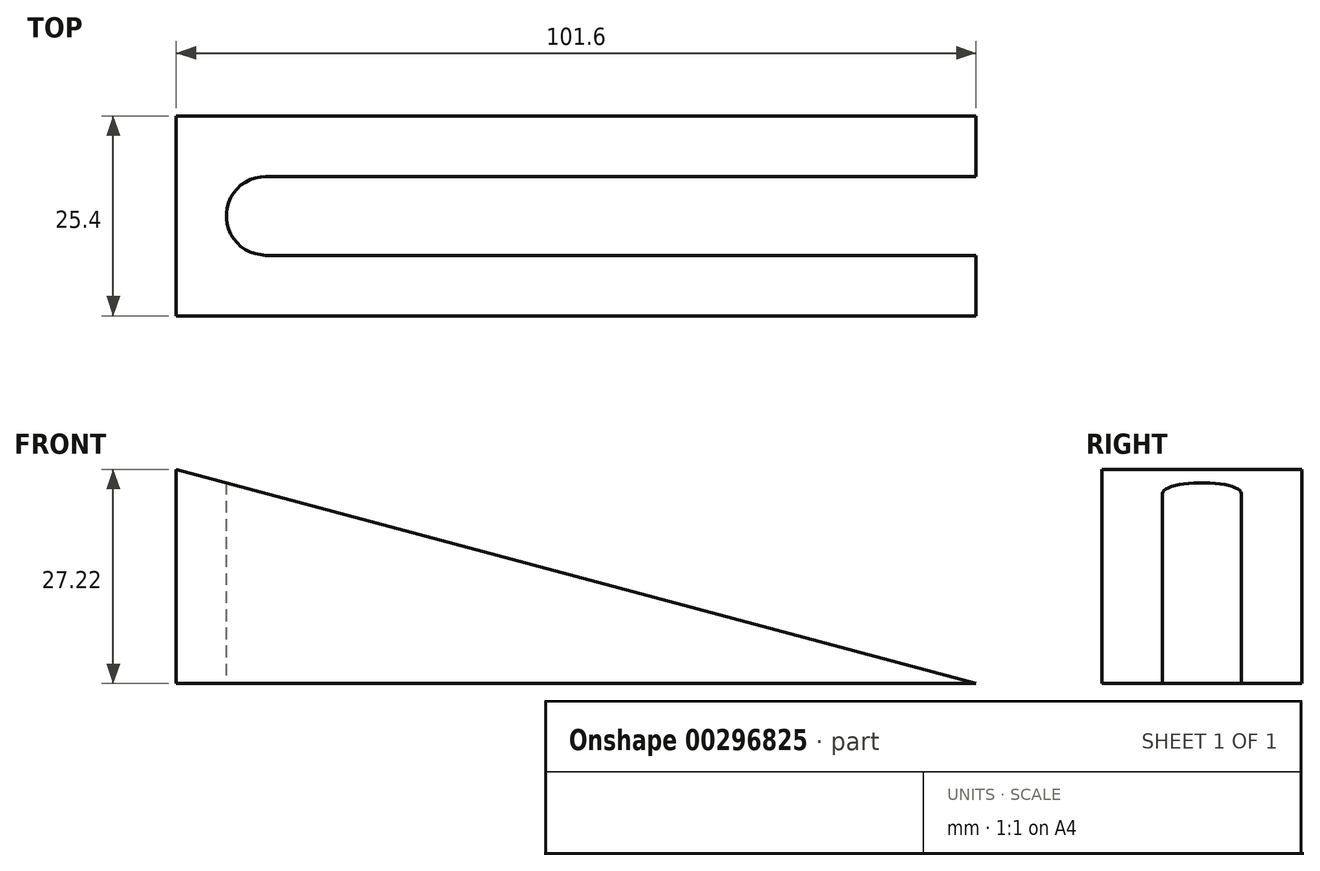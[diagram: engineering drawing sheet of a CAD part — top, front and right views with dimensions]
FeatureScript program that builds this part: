
annotation { "Feature Type Name" : "Feature", "Feature Type Description" : "" }
export const myFeature = defineFeature(function(context is Context, id is Id, definition is map)
    precondition{}
    {
        {
            var Q0;
            Q0=qCreatedBy(makeId("Front.planeOp"),FACE);
            var sketch = newSketch(context, id + "F0", { "sketchPlane" : qUnion([Q0])});
            skLineSegment(sketch, "E0", {"start": v(0, 0) * mm, "end": v(0, 27.22) * mm});
            skLineSegment(sketch, "E1", {"start": v(0, 27.22) * mm, "end": v(101.6, 0) * mm});
            skLineSegment(sketch, "E2", {"start": v(101.6, 0) * mm, "end": v(0, 0) * mm});
            skSolve(sketch);
        }
        {
            var Q0;
            Q0=makeQuery(id+"F0.imprint","IMPRINT",FACE,{"disambiguationData":[TD([[makeQuery(id+"F0.imprint","IMPRINT",EDGE,{"derivedFrom":sQuery(id+"F0.wireOp",EDGE,"E0")}),-1.0]])]});
            extrude(context, id + "F1", {"entities" : qUnion([Q0]), "depth" : 25.4 * mm});
        }
        {
            var Q0;
            Q0=makeQuery(id+"F1.opExtrude","SWEPT_FACE",FACE,{"disambiguationData":[OSD([sQuery(id+"F0.wireOp",EDGE,"E2")])]});
            var sketch = newSketch(context, id + "F2", { "sketchPlane" : qUnion([Q0])});
            skCircle(sketch, "E3", {"center": v(11.37, 12.7) * mm, "radius": 5.02 * mm});
            skPoint(sketch, "E3.centerSnap0", {"position": v(0, 12.7) * mm});
            skLineSegment(sketch, "E4", {"start": v(11.37, 17.72) * mm, "end": v(101.6, 17.72) * mm});
            skLineSegment(sketch, "E5", {"start": v(11.37, 7.68) * mm, "end": v(101.6, 7.68) * mm});
            skSolve(sketch);
        }
        {
            var Q0;
            {var subQ0=sQuery(id+"F2.wireOp",EDGE,"E3");var subQ1=makeQuery(id+"F2.imprint","INTERSECT",VERTEX,{"derivedFrom":[subQ0,sQuery(id+"F2.wireOp",EDGE,"E4")]});Q0=makeQuery(id+"F2.imprint","IMPRINT",FACE,{"disambiguationData":[TD([[makeQuery(id+"F2.imprint","IMPRINT",EDGE,{"disambiguationData":[TD([[subQ1,-1.0]])],"derivedFrom":subQ0}),1.0]])]});}
            var Q1;
            {var subQ0=sQuery(id+"F2.wireOp",EDGE,"E4");Q1=makeQuery(id+"F2.imprint","IMPRINT",FACE,{"disambiguationData":[TD([[makeQuery(id+"F2.imprint","IMPRINT",EDGE,{"derivedFrom":subQ0}),-1.0]])]});}
            extrude(context, id + "F3", {"entities" : qUnion([Q0, Q1]), "operationType" : NewBodyOperationType.REMOVE, "endBound" : BoundingType.UP_TO_NEXT, "oppositeDirection" : true, "depth" : 25.4 * mm});
        }
    });
